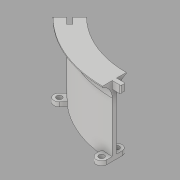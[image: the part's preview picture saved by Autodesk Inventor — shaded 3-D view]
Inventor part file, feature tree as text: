
AUTODESK INVENTOR PART (.ipt)
format: ipt  version: 2017 (Build 210142000, 142)  size: 247,296 bytes
history: native  units: in
note: dims shown in document units (in); Inventor stores cm internally (conversion verified against a paired STEP export)
features: extrude x5, sketch x5, fillet x2, projected_geometry x1
ambient origin geometry x8: Origin, YZ Plane, XZ Plane, XY Plane, X Axis, Y Axis, Z Axis, Center Point
bodies: Solid1 (feature_tree)
feature tree (13):
  extrude  "Extrusion1"  TaperAngle=45.0deg  [1 undecoded]
  extrude  "Extrusion2"  Depth=0.05in TaperAngle=0.0deg
  fillet  "Fillet1"  Radius=0.2in
  extrude  "Extrusion3"  Depth=0.45in
  extrude  "Extrusion4"  Depth=0.7in
  extrude  "Extrusion5"  Depth=0.05in
  fillet  "Fillet2"  Radius=0.25in
  sketch  "Sketch1"  dims[d0=1.1in d1=45.0deg]
  sketch  "Sketch2"  dims[d2=5.0in d3=0.05in d4=0.0in d5=0.2in]
  projected_geometry  "Projected Loop1"
  sketch  "Sketch3"  dims[d6=0.45in d7=0.45in]
  sketch  "Sketch4"  dims[d8=3.2in d9=0.0in d10=0.7in]
  sketch  "Sketch5"  dims[d11=0.25in d12=0.5in d13=0.25in d14=0.5in d15=0.2in d16=0.0in d17=0.45in d18=0.45in d19=0.35in d20=0.4in d21=0.0in d22=0.445in d23=0.445in d24=0.35in d25=0.4in d26=0.0in d27=0.05in]
note: 1 required parameter value undecoded (feature->parameter linkage not recoverable at this tier; creation-order binding heuristic only, values carry confidence <= 0.55)
